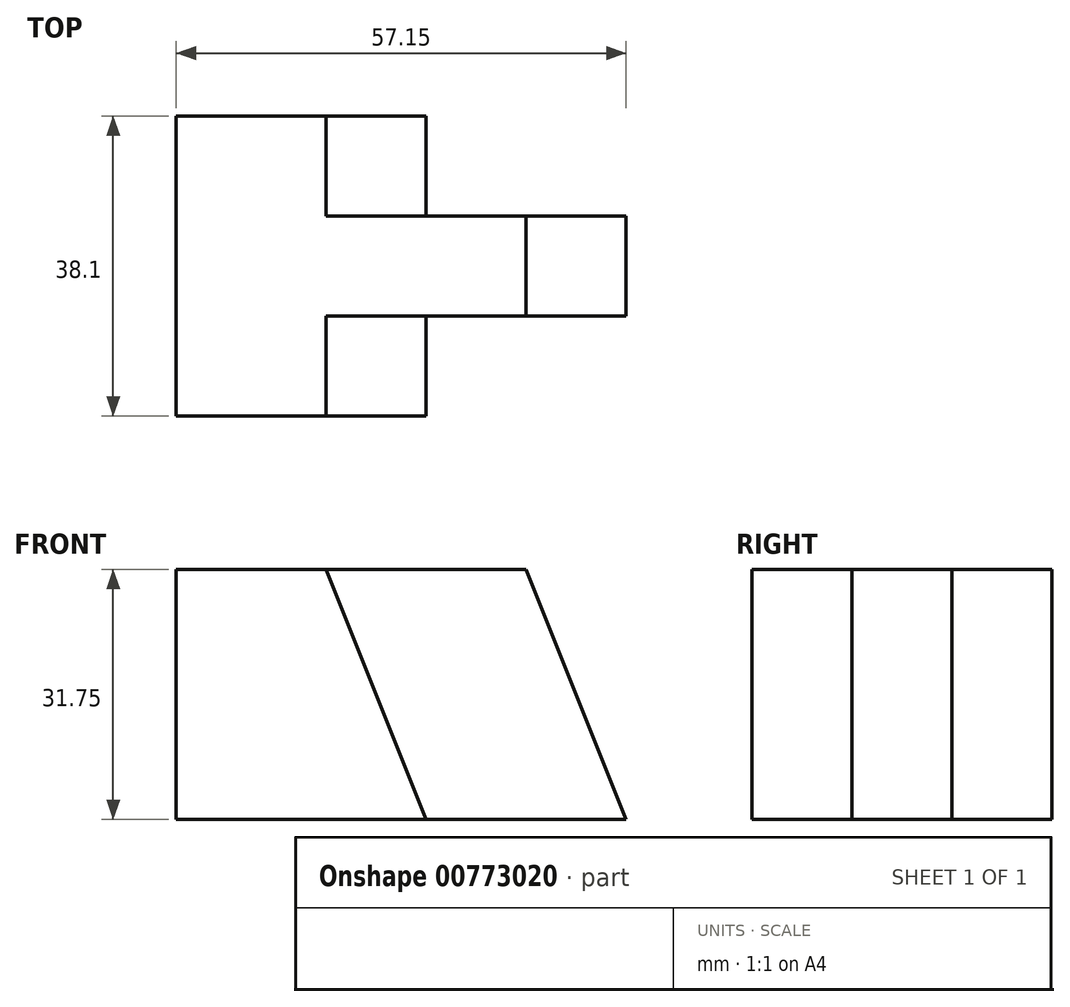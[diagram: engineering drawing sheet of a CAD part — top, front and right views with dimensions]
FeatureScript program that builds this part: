
annotation { "Feature Type Name" : "Feature", "Feature Type Description" : "" }
export const myFeature = defineFeature(function(context is Context, id is Id, definition is map)
    precondition{}
    {
        {
            var Q0;
            Q0=qCreatedBy(makeId("Front.planeOp"),FACE);
            var sketch = newSketch(context, id + "F0", { "sketchPlane" : qUnion([Q0])});
            skLineSegment(sketch, "E0", {"start": v(0, 0) * mm, "end": v(57.15, 0) * mm});
            skLineSegment(sketch, "E1", {"start": v(57.15, 0) * mm, "end": v(57.15, 31.75) * mm});
            skLineSegment(sketch, "E2", {"start": v(57.15, 31.75) * mm, "end": v(0, 31.75) * mm});
            skLineSegment(sketch, "E3", {"start": v(0, 31.75) * mm, "end": v(0, 0) * mm});
            skSolve(sketch);
        }
        {
            var Q0;
            Q0=makeQuery(id+"F0.imprint","IMPRINT",FACE,{"disambiguationData":[TD([[makeQuery(id+"F0.imprint","IMPRINT",EDGE,{"derivedFrom":sQuery(id+"F0.wireOp",EDGE,"E0")}),1.0]])]});
            extrude(context, id + "F1", {"entities" : qUnion([Q0]), "depth" : 38.1 * mm, "offsetDistance" : 25.4 * mm});
        }
        {
            var Q0;
            Q0=makeQuery(id+"F1.opExtrude","CAP_FACE",FACE,{"disambiguationData":[OSD([sQuery(id+"F0.wireOp",EDGE,"E0"),sQuery(id+"F0.wireOp",EDGE,"E1"),sQuery(id+"F0.wireOp",EDGE,"E2"),sQuery(id+"F0.wireOp",EDGE,"E3")])],"isStart":false});
            var sketch = newSketch(context, id + "F2", { "sketchPlane" : qUnion([Q0])});
            skLineSegment(sketch, "E4", {"start": v(0, 31.75) * mm, "end": v(19.05, 31.75) * mm});
            skLineSegment(sketch, "E5", {"start": v(0, 0) * mm, "end": v(31.75, 0) * mm});
            skLineSegment(sketch, "E6", {"start": v(31.75, 0) * mm, "end": v(19.05, 31.75) * mm});
            skSolve(sketch);
        }
        {
            var Q0;
            {var subQ0=sQuery(id+"F2.wireOp",EDGE,"E6");Q0=makeQuery(id+"F2.imprint","IMPRINT",FACE,{"disambiguationData":[TD([[makeQuery(id+"F2.imprint","IMPRINT",EDGE,{"derivedFrom":subQ0}),-1.0]])]});}
            extrude(context, id + "F3", {"entities" : qUnion([Q0]), "operationType" : NewBodyOperationType.REMOVE, "oppositeDirection" : true, "depth" : 12.7 * mm, "offsetDistance" : 25.4 * mm});
        }
        {
            var Q0;
            Q0=makeQuery(id+"F1.opExtrude","CAP_FACE",FACE,{"disambiguationData":[OSD([sQuery(id+"F0.wireOp",EDGE,"E0"),sQuery(id+"F0.wireOp",EDGE,"E1"),sQuery(id+"F0.wireOp",EDGE,"E2"),sQuery(id+"F0.wireOp",EDGE,"E3")])],"isStart":true});
            var sketch = newSketch(context, id + "F4", { "sketchPlane" : qUnion([Q0])});
            skLineSegment(sketch, "E7", {"start": v(0, 31.75) * mm, "end": v(-19.05, 31.75) * mm});
            skLineSegment(sketch, "E8", {"start": v(0, 0) * mm, "end": v(-31.75, 0) * mm});
            skLineSegment(sketch, "E9", {"start": v(-31.75, 0) * mm, "end": v(-19.05, 31.75) * mm});
            skSolve(sketch);
        }
        {
            var Q0;
            Q0 = qSketchRegion(id + "F4", true);
            var Q1;
            {var subQ0=sQuery(id+"F4.wireOp",EDGE,"E9");Q1=makeQuery(id+"F4.imprint","IMPRINT",FACE,{"disambiguationData":[TD([[makeQuery(id+"F4.imprint","IMPRINT",EDGE,{"derivedFrom":subQ0}),1.0]])]});}
            extrude(context, id + "F5", {"entities" : qUnion([Q0, Q1]), "operationType" : NewBodyOperationType.REMOVE, "oppositeDirection" : true, "depth" : 12.7 * mm, "offsetDistance" : 25.4 * mm});
        }
        {
            var Q0;
            Q0=makeQuery(id+"F3.boolean.opBoolean","COPY",FACE,{"derivedFrom":makeQuery(id+"F3.opExtrude","CAP_FACE",FACE,{"disambiguationData":[OSD([sQuery(id+"F0.wireOp",EDGE,"E0"),sQuery(id+"F0.wireOp",EDGE,"E1"),sQuery(id+"F0.wireOp",EDGE,"E2"),sQuery(id+"F2.wireOp",EDGE,"E6")])],"isStart":false})});
            var sketch = newSketch(context, id + "F6", { "sketchPlane" : qUnion([Q0])});
            skLineSegment(sketch, "E10", {"start": v(19.05, 31.75) * mm, "end": v(44.45, 31.75) * mm});
            skLineSegment(sketch, "E11", {"start": v(44.45, 31.75) * mm, "end": v(57.15, 0) * mm});
            skSolve(sketch);
        }
        {
            var Q0;
            {var subQ0=sQuery(id+"F6.wireOp",EDGE,"E11");Q0=makeQuery(id+"F6.imprint","IMPRINT",FACE,{"disambiguationData":[TD([[makeQuery(id+"F6.imprint","IMPRINT",EDGE,{"derivedFrom":subQ0}),1.0]])]});}
            extrude(context, id + "F7", {"entities" : qUnion([Q0]), "operationType" : NewBodyOperationType.REMOVE, "endBound" : BoundingType.THROUGH_ALL, "oppositeDirection" : true, "depth" : 25.4 * mm, "offsetDistance" : 25.4 * mm});
        }
    });
